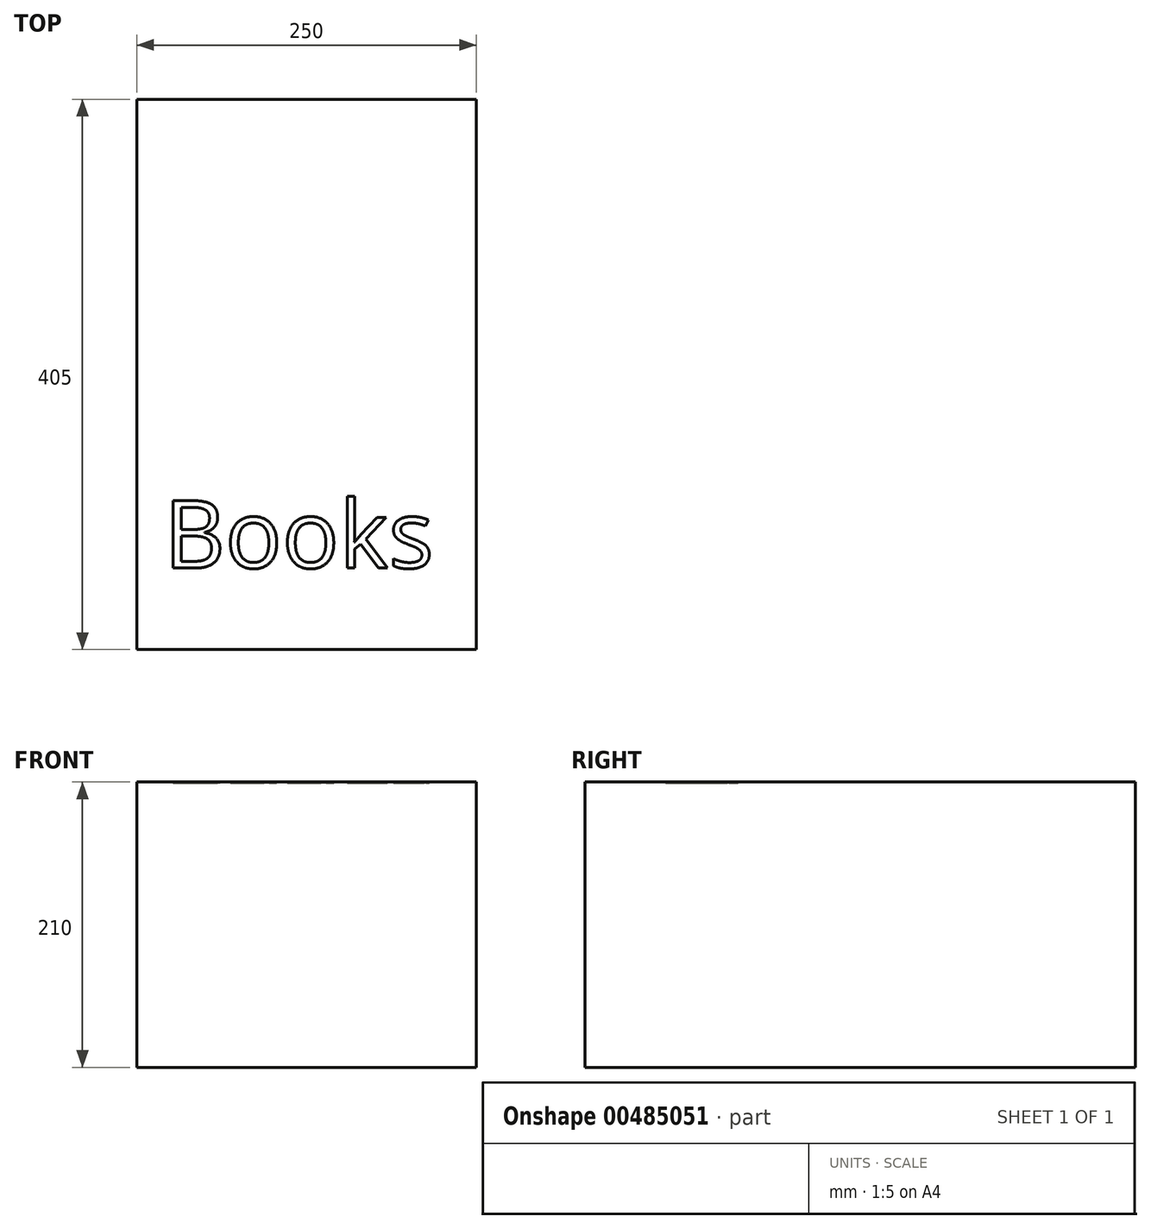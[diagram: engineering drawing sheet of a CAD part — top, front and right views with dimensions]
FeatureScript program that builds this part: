
annotation { "Feature Type Name" : "Feature", "Feature Type Description" : "" }
export const myFeature = defineFeature(function(context is Context, id is Id, definition is map)
    precondition{}
    {
        {
            var Q0;
            Q0=qCreatedBy(makeId("Top.planeOp"),FACE);
            var sketch = newSketch(context, id + "F0", { "sketchPlane" : qUnion([Q0])});
            skLineSegment(sketch, "E0.bottom", {"start": v(-125, -202.5) * mm, "end": v(125, -202.5) * mm});
            skLineSegment(sketch, "E0.top", {"start": v(-125, 202.5) * mm, "end": v(125, 202.5) * mm});
            skLineSegment(sketch, "E0.left", {"start": v(-125, -202.5) * mm, "end": v(-125, 202.5) * mm});
            skLineSegment(sketch, "E0.right", {"start": v(125, -202.5) * mm, "end": v(125, 202.5) * mm});
            skPoint(sketch, "E0.middle", {"position": v(0, 0) * mm});
            skSolve(sketch);
        }
        {
            var Q0;
            Q0 = qSketchRegion(id + "F0", true);
            extrude(context, id + "F1", {"entities" : qUnion([Q0]), "depth" : 210 * mm, "offsetDistance" : 25 * mm});
        }
        {
            var Q0;
            Q0=makeQuery(id+"F1.opExtrude","CAP_FACE",FACE,{"disambiguationData":[OSD([sQuery(id+"F0.wireOp",EDGE,"E0.bottom"),sQuery(id+"F0.wireOp",EDGE,"E0.top"),sQuery(id+"F0.wireOp",EDGE,"E0.left"),sQuery(id+"F0.wireOp",EDGE,"E0.right")])],"isStart":false});
            var sketch = newSketch(context, id + "F2", { "sketchPlane" : qUnion([Q0])});
            skText(sketch, "E1", { "text": "Books", "fontName": "OpenSans-Regular.ttf"});
            const initialGuessF2  = {"E1": [-0.105, -0.1425, 1, 0, 0.05]};
            skSetInitialGuess(sketch, initialGuessF2);
            skSolve(sketch);
        }
        {
            var Q0;
            Q0 = qSketchRegion(id + "F2", true);
            extrude(context, id + "F3", {"entities" : qUnion([Q0]), "operationType" : NewBodyOperationType.REMOVE, "oppositeDirection" : true, "depth" : 1 * mm, "offsetDistance" : 25 * mm});
        }
    });
